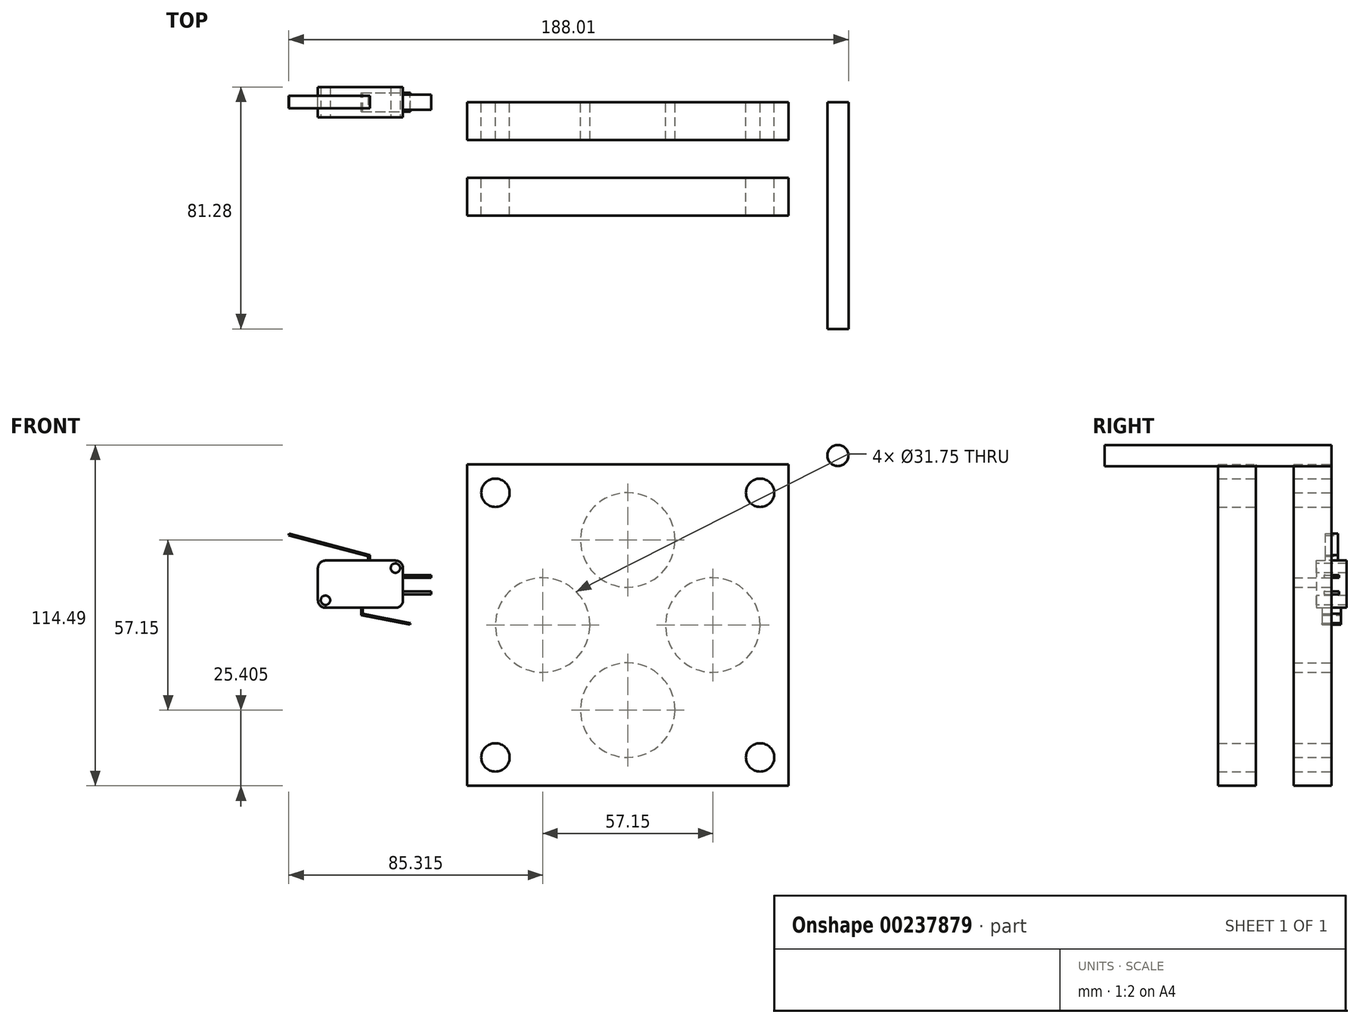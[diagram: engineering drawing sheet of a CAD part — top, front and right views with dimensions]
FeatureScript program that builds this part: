
annotation { "Feature Type Name" : "Feature", "Feature Type Description" : "" }
export const myFeature = defineFeature(function(context is Context, id is Id, definition is map)
    precondition{}
    {
        {
            var Q0;
            Q0=qCreatedBy(makeId("Front.planeOp"),FACE);
            var sketch = newSketch(context, id + "F0", { "sketchPlane" : qUnion([Q0])});
            skLineSegment(sketch, "E0.bottom", {"start": v(53.98, 53.98) * mm, "end": v(-53.98, 53.98) * mm});
            skLineSegment(sketch, "E0.top", {"start": v(53.98, -53.98) * mm, "end": v(-53.98, -53.98) * mm});
            skLineSegment(sketch, "E0.left", {"start": v(53.98, 53.98) * mm, "end": v(53.98, -53.98) * mm});
            skLineSegment(sketch, "E0.right", {"start": v(-53.98, 53.98) * mm, "end": v(-53.98, -53.98) * mm});
            skPoint(sketch, "E0.middle", {"position": v(0, 0) * mm});
            skCircle(sketch, "E1", {"center": v(0, 0) * mm, "radius": 28.58 * mm, "construction": true});
            skCircle(sketch, "E2", {"center": v(0, 28.58) * mm, "radius": 15.88 * mm});
            skCircle(sketch, "E3", {"center": v(28.58, 0) * mm, "radius": 15.88 * mm});
            skCircle(sketch, "E4", {"center": v(0, -28.58) * mm, "radius": 15.88 * mm});
            skCircle(sketch, "E5", {"center": v(-28.58, 0) * mm, "radius": 15.88 * mm});
            skCircle(sketch, "E6", {"center": v(-44.45, 44.45) * mm, "radius": 4.76 * mm});
            skCircle(sketch, "E7", {"center": v(44.45, 44.45) * mm, "radius": 4.76 * mm});
            skLineSegment(sketch, "E8", {"start": v(-44.45, 44.45) * mm, "end": v(44.45, 44.45) * mm});
            skCircle(sketch, "E9.MirrorC", {"center": v(-44.45, -44.45) * mm, "radius": 4.76 * mm});
            skCircle(sketch, "E10.MirrorC", {"center": v(44.45, -44.45) * mm, "radius": 4.76 * mm});
            skSolve(sketch);
        }
        {
            var Q0;
            Q0 = qSketchRegion(id + "F0", true);
            extrude(context, id + "F1", {"entities" : qUnion([Q0]), "depth" : 12.7 * mm});
        }
        {
            var Q0;
            Q0=qCreatedBy(makeId("Front.planeOp"),FACE);
            cPlane(context, id + "F2", {"entities" : qUnion([Q0]), "cplaneType" : CPlaneType.OFFSET, "offset" : 25.4 * mm, "width" : 152.4 * mm, "height" : 152.4 * mm});
        }
        {
            var Q0;
            Q0=qCreatedBy(id+"F2.planeOp",FACE);
            var sketch = newSketch(context, id + "F3", { "sketchPlane" : qUnion([Q0])});
            skLineSegment(sketch, "E11.bottom", {"start": v(53.97, 53.98) * mm, "end": v(-53.98, 53.98) * mm});
            skLineSegment(sketch, "E11.top", {"start": v(53.98, -53.98) * mm, "end": v(-53.97, -53.98) * mm});
            skLineSegment(sketch, "E11.left", {"start": v(53.97, 53.98) * mm, "end": v(53.98, -53.98) * mm});
            skLineSegment(sketch, "E11.right", {"start": v(-53.98, 53.98) * mm, "end": v(-53.97, -53.98) * mm});
            skPoint(sketch, "E11.middle", {"position": v(0, 0) * mm});
            skCircle(sketch, "E12", {"center": v(44.45, 44.45) * mm, "radius": 4.76 * mm});
            skCircle(sketch, "E13.MirrorC", {"center": v(-44.45, 44.45) * mm, "radius": 4.76 * mm});
            skCircle(sketch, "E14.MirrorC", {"center": v(-44.45, -44.45) * mm, "radius": 4.76 * mm});
            skCircle(sketch, "E15.MirrorC", {"center": v(44.45, -44.45) * mm, "radius": 4.76 * mm});
            skSolve(sketch);
        }
        {
            var Q0;
            Q0 = qSketchRegion(id + "F3", true);
            extrude(context, id + "F4", {"entities" : qUnion([Q0]), "depth" : 12.7 * mm});
        }
        {
            var Q0;
            Q0=qCreatedBy(makeId("Front.planeOp"),FACE);
            var sketch = newSketch(context, id + "F5", { "sketchPlane" : qUnion([Q0])});
            skCircle(sketch, "E16", {"center": v(70.56, 56.95) * mm, "radius": 3.56 * mm});
            skSolve(sketch);
        }
        {
            var Q0;
            Q0=makeQuery(id+"F5.imprint","IMPRINT",FACE,{"disambiguationData":[TD([[makeQuery(id+"F5.imprint","IMPRINT",EDGE,{"derivedFrom":sQuery(id+"F5.wireOp",EDGE,"E16")}),1.0]])]});
            var Q1;
            Q1=sQuery(id+"F5.wireOp",EDGE,"E16");
            extrude(context, id + "F6", {"entities" : qUnion([Q0]), "surfaceEntities" : qUnion([Q1]), "depth" : 76.2 * mm, "offsetDistance" : 25.4 * mm});
        }
        {
            var Q0;
            Q0=qCreatedBy(makeId("Front.planeOp"),FACE);
            var sketch = newSketch(context, id + "F7", { "sketchPlane" : qUnion([Q0])});
            skLineSegment(sketch, "E17.bottom", {"start": v(-104.07, 21.67) * mm, "end": v(-75.5, 21.67) * mm});
            skLineSegment(sketch, "E17.top", {"start": v(-104.07, 5.8) * mm, "end": v(-75.5, 5.8) * mm});
            skLineSegment(sketch, "E17.left", {"start": v(-104.07, 21.67) * mm, "end": v(-104.07, 5.8) * mm});
            skLineSegment(sketch, "E17.right", {"start": v(-75.5, 21.67) * mm, "end": v(-75.5, 5.8) * mm});
            skSolve(sketch);
        }
        {
            var Q0;
            Q0 = qSketchRegion(id + "F7", true);
            extrude(context, id + "F8", {"entities" : qUnion([Q0]), "endBound" : BoundingType.SYMMETRIC, "depth" : 10.16 * mm, "offsetDistance" : 25.4 * mm});
        }
        {
            var Q0;
            Q0=makeQuery(id+"F8.opExtrude","SWEPT_EDGE",EDGE,{"disambiguationData":[OSD([sQuery(id+"F7.wireOp",EDGE,"E17.bottom"),sQuery(id+"F7.wireOp",EDGE,"E17.left")])]});
            var Q1;
            Q1=makeQuery(id+"F8.opExtrude","SWEPT_EDGE",EDGE,{"disambiguationData":[OSD([sQuery(id+"F7.wireOp",EDGE,"E17.top"),sQuery(id+"F7.wireOp",EDGE,"E17.left")])]});
            var Q2;
            Q2=makeQuery(id+"F8.opExtrude","SWEPT_EDGE",EDGE,{"disambiguationData":[OSD([sQuery(id+"F7.wireOp",EDGE,"E17.top"),sQuery(id+"F7.wireOp",EDGE,"E17.right")])]});
            var Q3;
            Q3=makeQuery(id+"F8.opExtrude","SWEPT_EDGE",EDGE,{"disambiguationData":[OSD([sQuery(id+"F7.wireOp",EDGE,"E17.bottom"),sQuery(id+"F7.wireOp",EDGE,"E17.right")])]});
            fillet(context, id + "F9", {"entities" : qUnion([Q0, Q1, Q2, Q3]), "radius" : 2.54 * mm, "tangentPropagation" : true, "allowEdgeOverflow" : false});
        }
        {
            var Q0;
            Q0=makeQuery(id+"F8.opExtrude","CAP_FACE",FACE,{"disambiguationData":[OSD([sQuery(id+"F7.wireOp",EDGE,"E17.bottom"),sQuery(id+"F7.wireOp",EDGE,"E17.top"),sQuery(id+"F7.wireOp",EDGE,"E17.left"),sQuery(id+"F7.wireOp",EDGE,"E17.right")])],"isStart":false});
            var sketch = newSketch(context, id + "F10", { "sketchPlane" : qUnion([Q0])});
            skCircle(sketch, "E18", {"center": v(-101.53, 8.34) * mm, "radius": 1.59 * mm});
            skCircle(sketch, "E19", {"center": v(-78.04, 19.13) * mm, "radius": 1.59 * mm});
            skSolve(sketch);
        }
        {
            var Q0;
            Q0 = qSketchRegion(id + "F10", true);
            extrude(context, id + "F11", {"entities" : qUnion([Q0]), "operationType" : NewBodyOperationType.REMOVE, "oppositeDirection" : true, "depth" : 25.4 * mm, "offsetDistance" : 25.4 * mm});
        }
        {
            var Q0;
            Q0=qCreatedBy(makeId("Front.planeOp"),FACE);
            var sketch = newSketch(context, id + "F12", { "sketchPlane" : qUnion([Q0])});
            skLineSegment(sketch, "E20", {"start": v(-89.47, 6.13) * mm, "end": v(-89.47, 3.35) * mm});
            skLineSegment(sketch, "E21", {"start": v(-89.47, 3.35) * mm, "end": v(-73.09, 0.11) * mm});
            skLineSegment(sketch, "E22.0", {"start": v(-88.96, 3.76) * mm, "end": v(-72.99, 0.61) * mm});
            skLineSegment(sketch, "E22.1", {"start": v(-88.96, 6.13) * mm, "end": v(-88.96, 3.76) * mm});
            skLineSegment(sketch, "E23", {"start": v(-73.09, 0.11) * mm, "end": v(-72.99, 0.61) * mm});
            skLineSegment(sketch, "E24", {"start": v(-89.47, 6.13) * mm, "end": v(-88.96, 6.13) * mm});
            skSolve(sketch);
        }
        {
            var Q0;
            Q0=makeQuery(id+"F12.imprint","IMPRINT",FACE,{"disambiguationData":[TD([[makeQuery(id+"F12.imprint","IMPRINT",EDGE,{"derivedFrom":sQuery(id+"F12.wireOp",EDGE,"E20")}),1.0]])]});
            extrude(context, id + "F13", {"entities" : qUnion([Q0]), "operationType" : NewBodyOperationType.ADD, "endBound" : BoundingType.SYMMETRIC, "depth" : 6.35 * mm, "offsetDistance" : 25.4 * mm});
        }
        {
            var Q0;
            Q0=qCreatedBy(makeId("Front.planeOp"),FACE);
            var sketch = newSketch(context, id + "F14", { "sketchPlane" : qUnion([Q0])});
            skLineSegment(sketch, "E25.bottom", {"start": v(-76.16, 16.83) * mm, "end": v(-66.01, 16.83) * mm});
            skLineSegment(sketch, "E25.top", {"start": v(-76.16, 15.84) * mm, "end": v(-66.01, 15.84) * mm});
            skLineSegment(sketch, "E25.left", {"start": v(-76.16, 16.83) * mm, "end": v(-76.16, 15.84) * mm});
            skLineSegment(sketch, "E25.right", {"start": v(-66.01, 16.83) * mm, "end": v(-66.01, 15.84) * mm});
            skLineSegment(sketch, "E26.bottom", {"start": v(-76.34, 11.3) * mm, "end": v(-66.01, 11.3) * mm});
            skLineSegment(sketch, "E26.top", {"start": v(-76.34, 10.3) * mm, "end": v(-66.01, 10.3) * mm});
            skLineSegment(sketch, "E26.left", {"start": v(-76.34, 11.3) * mm, "end": v(-76.34, 10.3) * mm});
            skLineSegment(sketch, "E26.right", {"start": v(-66.01, 11.3) * mm, "end": v(-66.01, 10.3) * mm});
            skSolve(sketch);
        }
        {
            var Q0;
            Q0 = qSketchRegion(id + "F14", true);
            extrude(context, id + "F15", {"entities" : qUnion([Q0]), "operationType" : NewBodyOperationType.ADD, "endBound" : BoundingType.SYMMETRIC, "depth" : 5.08 * mm, "offsetDistance" : 25.4 * mm});
        }
        {
            var Q0;
            Q0=qCreatedBy(makeId("Front.planeOp"),FACE);
            var sketch = newSketch(context, id + "F16", { "sketchPlane" : qUnion([Q0])});
            skLineSegment(sketch, "E27", {"start": v(-87.18, 19.67) * mm, "end": v(-87.18, 23.08) * mm});
            skLineSegment(sketch, "E28", {"start": v(-87.18, 23.08) * mm, "end": v(-113.9, 30.15) * mm});
            skLineSegment(sketch, "E29.0", {"start": v(-86.55, 23.57) * mm, "end": v(-113.73, 30.76) * mm});
            skLineSegment(sketch, "E29.1", {"start": v(-86.55, 19.67) * mm, "end": v(-86.55, 23.57) * mm});
            skLineSegment(sketch, "E30", {"start": v(-113.9, 30.15) * mm, "end": v(-113.73, 30.76) * mm});
            skLineSegment(sketch, "E31", {"start": v(-87.18, 19.67) * mm, "end": v(-86.55, 19.67) * mm});
            skSolve(sketch);
        }
        {
            var Q0;
            Q0 = qSketchRegion(id + "F16", true);
            extrude(context, id + "F17", {"entities" : qUnion([Q0]), "operationType" : NewBodyOperationType.ADD, "endBound" : BoundingType.SYMMETRIC, "depth" : 4.2 * mm, "offsetDistance" : 25.4 * mm});
        }
    });
